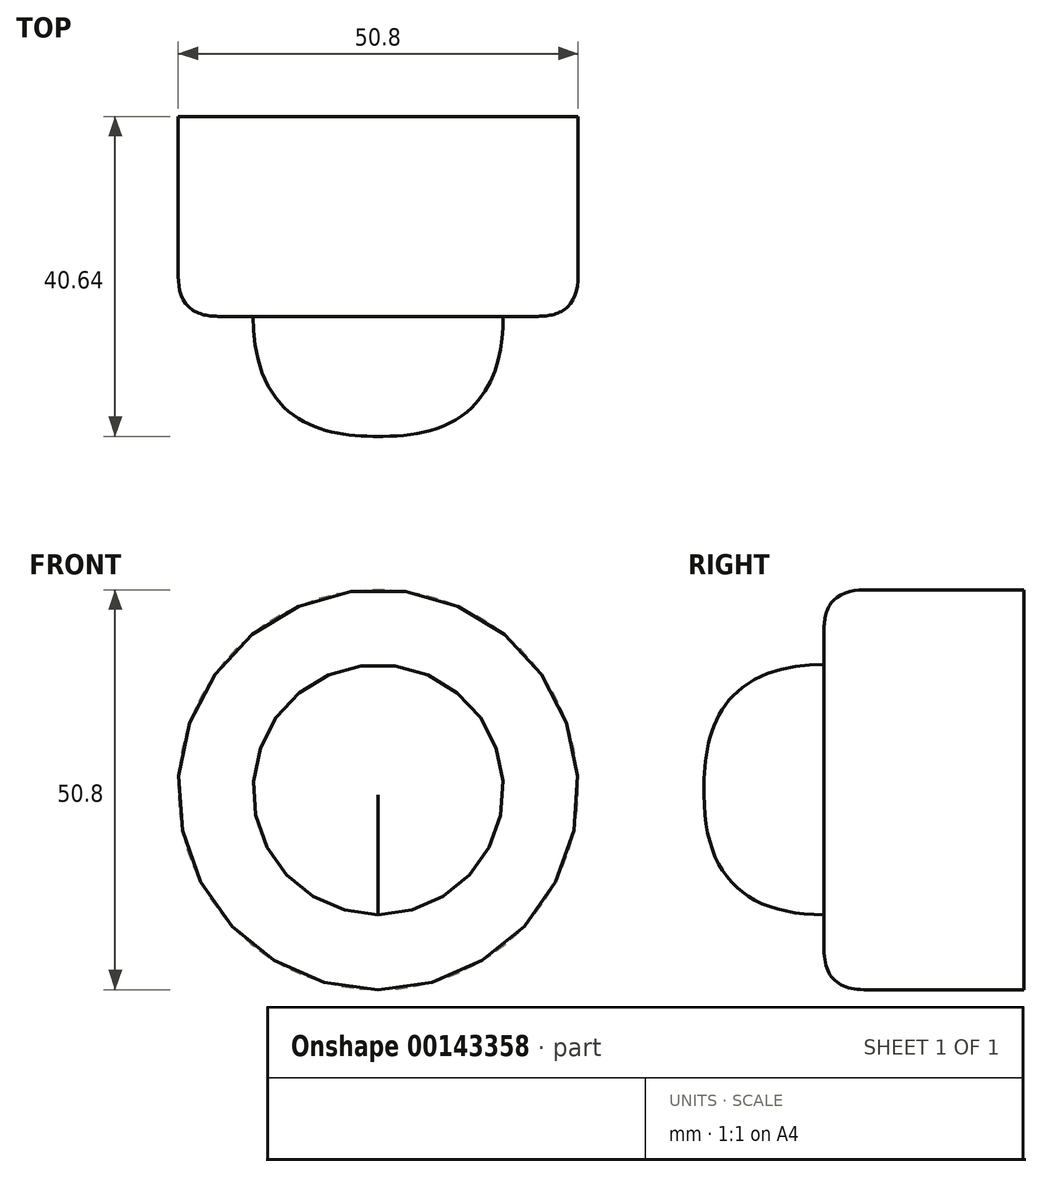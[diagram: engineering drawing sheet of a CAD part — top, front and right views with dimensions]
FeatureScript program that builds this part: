
annotation { "Feature Type Name" : "Feature", "Feature Type Description" : "" }
export const myFeature = defineFeature(function(context is Context, id is Id, definition is map)
    precondition{}
    {
        {
            var Q0;
            Q0=qCreatedBy(makeId("Front.planeOp"),FACE);
            var sketch = newSketch(context, id + "F0", { "sketchPlane" : qUnion([Q0])});
            skCircle(sketch, "E0", {"center": v(0, 0) * mm, "radius": 25.4 * mm});
            skSolve(sketch);
        }
        {
            var Q0;
            Q0 = qSketchRegion(id + "F0", true);
            extrude(context, id + "F1", {"entities" : qUnion([Q0]), "depth" : 25.4 * mm});
        }
        {
            var Q0;
            Q0=makeQuery(id+"F1.opExtrude","CAP_FACE",FACE,{"disambiguationData":[OSD([sQuery(id+"F0.wireOp",EDGE,"E0")])],"isStart":false});
            var sketch = newSketch(context, id + "F2", { "sketchPlane" : qUnion([Q0])});
            skCircle(sketch, "E1", {"center": v(0, 0) * mm, "radius": 15.88 * mm});
            skSolve(sketch);
        }
        {
            var Q0;
            Q0 = qSketchRegion(id + "F2", true);
            extrude(context, id + "F3", {"entities" : qUnion([Q0]), "operationType" : NewBodyOperationType.ADD, "depth" : 15.24 * mm});
        }
        {
            var Q0;
            Q0=makeQuery(id+"F1.opExtrude","CAP_EDGE",EDGE,{"disambiguationData":[OSD([sQuery(id+"F0.wireOp",EDGE,"E0")])],"isStart":false});
            fillet(context, id + "F4", {"entities" : qUnion([Q0]), "radius" : 5.08 * mm, "tangentPropagation" : true, "rho" : 0.5, "crossSection" : FilletCrossSection.CONIC, "allowEdgeOverflow" : false});
        }
        {
            var Q0;
            Q0=makeQuery(id+"F3.opExtrude","CAP_EDGE",EDGE,{"disambiguationData":[OSD([sQuery(id+"F2.wireOp",EDGE,"E1")])],"isStart":false});
            fillet(context, id + "F5", {"entities" : qUnion([Q0]), "radius" : 15.24 * mm, "tangentPropagation" : true, "rho" : 0.5, "crossSection" : FilletCrossSection.CONIC, "allowEdgeOverflow" : false});
        }
    });
